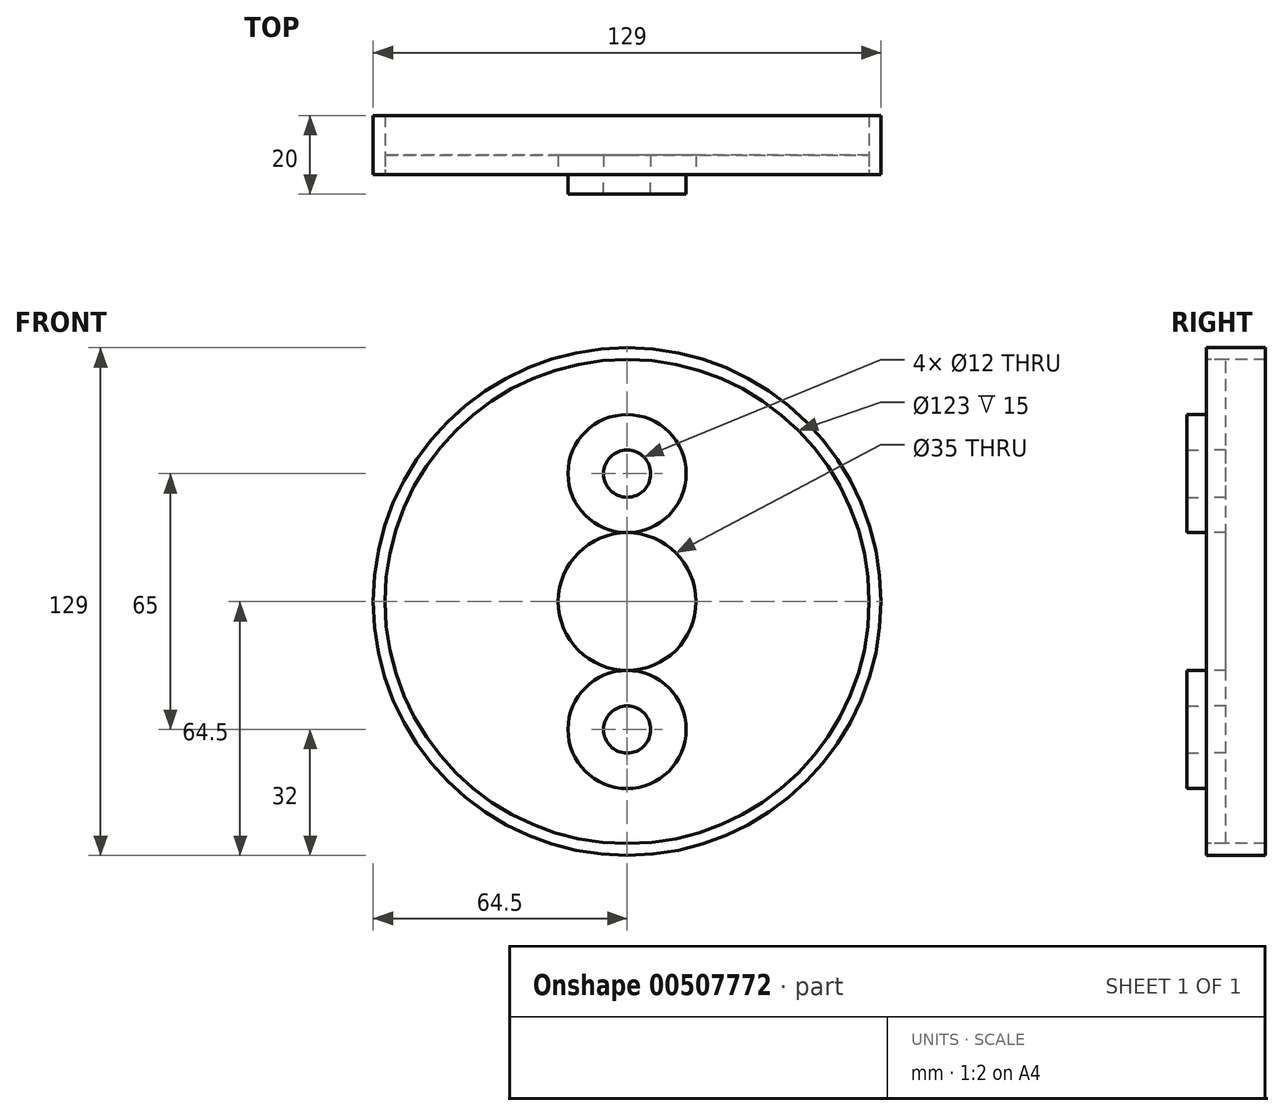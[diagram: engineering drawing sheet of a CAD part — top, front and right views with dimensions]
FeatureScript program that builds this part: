
annotation { "Feature Type Name" : "Feature", "Feature Type Description" : "" }
export const myFeature = defineFeature(function(context is Context, id is Id, definition is map)
    precondition{}
    {
        {
            var Q0;
            Q0=qCreatedBy(makeId("Front.planeOp"),FACE);
            var sketch = newSketch(context, id + "F0", { "sketchPlane" : qUnion([Q0])});
            skCircle(sketch, "E0", {"center": v(0, 0) * mm, "radius": 17.5 * mm});
            skCircle(sketch, "E1", {"center": v(0, 0) * mm, "radius": 61.5 * mm});
            skCircle(sketch, "E2.0", {"center": v(0, 0) * mm, "radius": 64.5 * mm});
            skCircle(sketch, "E3", {"center": v(0, 32.5) * mm, "radius": 6 * mm});
            skCircle(sketch, "E4", {"center": v(0, -32.5) * mm, "radius": 6 * mm});
            skLineSegment(sketch, "E5", {"start": v(-17.5, 0) * mm, "end": v(17.5, 0) * mm, "construction": true});
            skCircle(sketch, "E6", {"center": v(0, 32.5) * mm, "radius": 15 * mm});
            skCircle(sketch, "E7.MirrorC", {"center": v(0, -32.5) * mm, "radius": 15 * mm});
            skSolve(sketch);
        }
        {
            var Q0;
            Q0=makeQuery(id+"F0.imprint","IMPRINT",FACE,{"disambiguationData":[TD([[makeQuery(id+"F0.imprint","IMPRINT",EDGE,{"derivedFrom":sQuery(id+"F0.wireOp",EDGE,"E1")}),1.0]])]});
            var Q1;
            Q1=makeQuery(id+"F0.imprint","IMPRINT",FACE,{"disambiguationData":[TD([[makeQuery(id+"F0.imprint","IMPRINT",EDGE,{"derivedFrom":sQuery(id+"F0.wireOp",EDGE,"E3")}),-1.0]])]});
            var Q2;
            Q2=makeQuery(id+"F0.imprint","IMPRINT",FACE,{"disambiguationData":[TD([[makeQuery(id+"F0.imprint","IMPRINT",EDGE,{"derivedFrom":sQuery(id+"F0.wireOp",EDGE,"E4")}),-1.0]])]});
            extrude(context, id + "F1", {"entities" : qUnion([Q0, Q1, Q2]), "oppositeDirection" : true, "depth" : 5 * mm});
        }
        {
            var Q0;
            Q0=makeQuery(id+"F0.imprint","IMPRINT",FACE,{"disambiguationData":[TD([[makeQuery(id+"F0.imprint","IMPRINT",EDGE,{"derivedFrom":sQuery(id+"F0.wireOp",EDGE,"E1")}),-1.0]])]});
            extrude(context, id + "F2", {"entities" : qUnion([Q0]), "oppositeDirection" : true, "depth" : 15 * mm});
        }
        {
            var Q0;
            Q0=makeQuery(id+"F0.imprint","IMPRINT",FACE,{"disambiguationData":[TD([[makeQuery(id+"F0.imprint","IMPRINT",EDGE,{"derivedFrom":sQuery(id+"F0.wireOp",EDGE,"E3")}),-1.0]])]});
            var Q1;
            Q1=makeQuery(id+"F0.imprint","IMPRINT",FACE,{"disambiguationData":[TD([[makeQuery(id+"F0.imprint","IMPRINT",EDGE,{"derivedFrom":sQuery(id+"F0.wireOp",EDGE,"E4")}),-1.0]])]});
            extrude(context, id + "F3", {"entities" : qUnion([Q0, Q1]), "depth" : 5 * mm});
        }
    });
